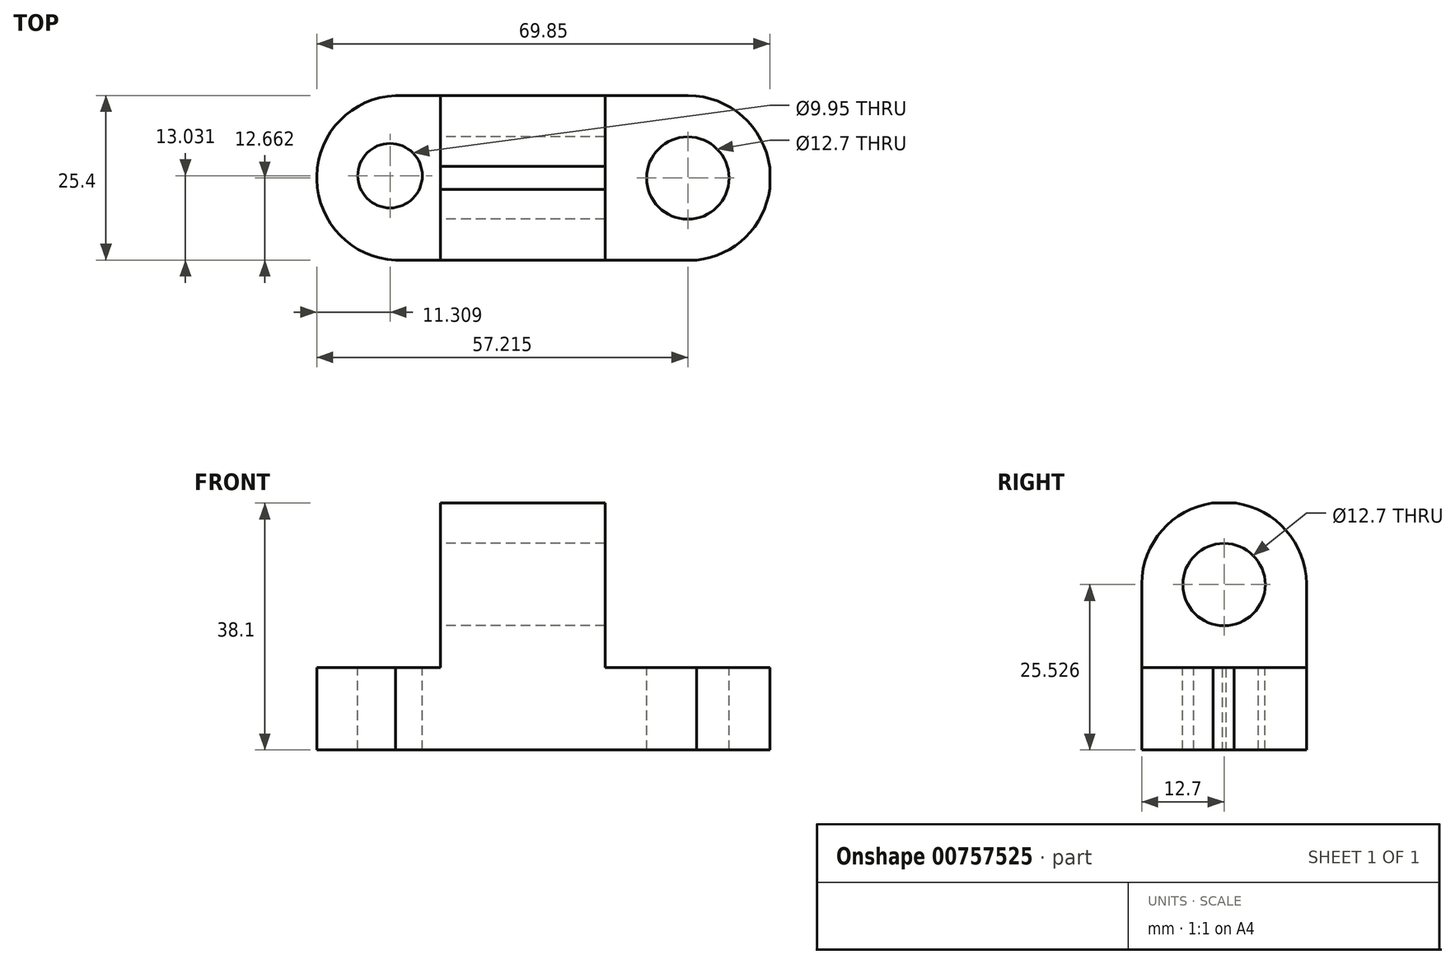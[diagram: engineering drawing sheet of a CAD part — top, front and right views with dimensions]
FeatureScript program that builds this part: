
annotation { "Feature Type Name" : "Feature", "Feature Type Description" : "" }
export const myFeature = defineFeature(function(context is Context, id is Id, definition is map)
    precondition{}
    {
        {
            var Q0;
            Q0=qCreatedBy(makeId("Front.planeOp"),FACE);
            var sketch = newSketch(context, id + "F0", { "sketchPlane" : qUnion([Q0])});
            skLineSegment(sketch, "E0", {"start": v(0, 0) * mm, "end": v(-69.85, 0) * mm});
            skLineSegment(sketch, "E1", {"start": v(-69.85, 0) * mm, "end": v(-69.85, 12.7) * mm});
            skLineSegment(sketch, "E2", {"start": v(-69.85, 12.7) * mm, "end": v(-50.8, 12.7) * mm});
            skLineSegment(sketch, "E3", {"start": v(-50.8, 12.7) * mm, "end": v(-50.8, 38.1) * mm});
            skLineSegment(sketch, "E4", {"start": v(-50.8, 38.1) * mm, "end": v(-25.4, 38.1) * mm});
            skLineSegment(sketch, "E5", {"start": v(-25.4, 38.1) * mm, "end": v(-25.4, 12.7) * mm});
            skLineSegment(sketch, "E6", {"start": v(-25.4, 12.7) * mm, "end": v(0, 12.7) * mm});
            skLineSegment(sketch, "E7", {"start": v(0, 12.7) * mm, "end": v(0, 0) * mm});
            skSolve(sketch);
        }
        {
            var Q0;
            Q0 = qSketchRegion(id + "F0", true);
            extrude(context, id + "F1", {"entities" : qUnion([Q0]), "depth" : 25.4 * mm, "offsetDistance" : 25.4 * mm});
        }
        {
            var Q0;
            Q0=makeQuery(id+"F1.opExtrude","SWEPT_FACE",FACE,{"disambiguationData":[OSD([sQuery(id+"F0.wireOp",EDGE,"E0")])]});
            var sketch = newSketch(context, id + "F2", { "sketchPlane" : qUnion([Q0])});
            skArc(sketch, "E8", {"start": v(-12.7, 0) * mm, "mid": v(0.09, 13.4) * mm, "end": v(-14.02, 25.4) * mm});
            skArc(sketch, "E9", {"start": v(-56.58, 25.4) * mm, "mid": v(-69.84, 13.24) * mm, "end": v(-57.66, 0) * mm});
            skSolve(sketch);
        }
        {
            var Q0;
            {var subQ0=sQuery(id+"F2.wireOp",EDGE,"E8");var subQ1=sQuery(id+"F0.wireOp",EDGE,"E0");var subQ4=makeQuery(id+"F1.opExtrude","CAP_EDGE",EDGE,{"disambiguationData":[OSD([subQ1])],"isStart":false});var subQ5=makeQuery(id+"F2.imprint","INTERSECT",VERTEX,{"disambiguationData":[OD(1.0)],"derivedFrom":[subQ4,subQ0]});Q0=makeQuery(id+"F2.imprint","IMPRINT",FACE,{"disambiguationData":[TD([[makeQuery(id+"F2.imprint","IMPRINT",EDGE,{"disambiguationData":[TD([[subQ5,1.0]])],"derivedFrom":subQ0}),-1.0]])]});}
            var Q1;
            {var subQ0=sQuery(id+"F2.wireOp",EDGE,"E8");var subQ1=sQuery(id+"F0.wireOp",EDGE,"E0");var subQ2=makeQuery(id+"F1.opExtrude","CAP_EDGE",EDGE,{"disambiguationData":[OSD([subQ1])],"isStart":true});var subQ3=makeQuery(id+"F2.imprint","INTERSECT",VERTEX,{"disambiguationData":[OD(1.0)],"derivedFrom":[subQ2,subQ0]});Q1=makeQuery(id+"F2.imprint","IMPRINT",FACE,{"disambiguationData":[TD([[makeQuery(id+"F2.imprint","IMPRINT",EDGE,{"disambiguationData":[TD([[subQ3,-1.0]])],"derivedFrom":subQ0}),-1.0]])]});}
            var Q2;
            {var subQ0=sQuery(id+"F2.wireOp",EDGE,"E9");var subQ1=sQuery(id+"F0.wireOp",EDGE,"E0");var subQ2=makeQuery(id+"F1.opExtrude","CAP_EDGE",EDGE,{"disambiguationData":[OSD([subQ1])],"isStart":true});var subQ3=makeQuery(id+"F2.imprint","INTERSECT",VERTEX,{"derivedFrom":[subQ2,subQ0]});Q2=makeQuery(id+"F2.imprint","IMPRINT",FACE,{"disambiguationData":[TD([[makeQuery(id+"F2.imprint","IMPRINT",EDGE,{"disambiguationData":[TD([[subQ3,1.0]])],"derivedFrom":subQ0}),-1.0]])]});}
            var Q3;
            {var subQ0=sQuery(id+"F2.wireOp",EDGE,"E9");var subQ1=sQuery(id+"F0.wireOp",EDGE,"E0");var subQ2=makeQuery(id+"F1.opExtrude","CAP_EDGE",EDGE,{"disambiguationData":[OSD([subQ1])],"isStart":false});var subQ3=makeQuery(id+"F2.imprint","INTERSECT",VERTEX,{"disambiguationData":[OD(1.0)],"derivedFrom":[subQ2,subQ0]});Q3=makeQuery(id+"F2.imprint","IMPRINT",FACE,{"disambiguationData":[TD([[makeQuery(id+"F2.imprint","IMPRINT",EDGE,{"disambiguationData":[TD([[subQ3,-1.0]])],"derivedFrom":subQ0}),-1.0]])]});}
            extrude(context, id + "F3", {"entities" : qUnion([Q0, Q1, Q2, Q3]), "operationType" : NewBodyOperationType.REMOVE, "endBound" : BoundingType.THROUGH_ALL, "oppositeDirection" : true, "depth" : 25.4 * mm, "offsetDistance" : 25.4 * mm});
        }
        {
            var Q0;
            Q0=makeQuery(id+"F1.opExtrude","SWEPT_FACE",FACE,{"disambiguationData":[OSD([sQuery(id+"F0.wireOp",EDGE,"E5")])]});
            var sketch = newSketch(context, id + "F4", { "sketchPlane" : qUnion([Q0])});
            skArc(sketch, "E10", {"start": v(0, 25.4) * mm, "mid": v(-12.7, 38.23) * mm, "end": v(-25.4, 25.4) * mm});
            skSolve(sketch);
        }
        {
            var Q0;
            {var subQ0=sQuery(id+"F4.wireOp",EDGE,"E10");var subQ1=sQuery(id+"F0.wireOp",EDGE,"E5");var subQ4=makeQuery(id+"F1.opExtrude","CAP_EDGE",EDGE,{"disambiguationData":[OSD([subQ1])],"isStart":false});var subQ5=makeQuery(id+"F4.imprint","INTERSECT",VERTEX,{"disambiguationData":[OD(1.0)],"derivedFrom":[subQ4,subQ0]});Q0=makeQuery(id+"F4.imprint","IMPRINT",FACE,{"disambiguationData":[TD([[makeQuery(id+"F4.imprint","IMPRINT",EDGE,{"disambiguationData":[TD([[subQ5,1.0]])],"derivedFrom":subQ0}),-1.0]])]});}
            var Q1;
            {var subQ0=sQuery(id+"F4.wireOp",EDGE,"E10");var subQ1=sQuery(id+"F0.wireOp",EDGE,"E5");var subQ2=makeQuery(id+"F1.opExtrude","CAP_EDGE",EDGE,{"disambiguationData":[OSD([subQ1])],"isStart":true});var subQ3=makeQuery(id+"F4.imprint","INTERSECT",VERTEX,{"disambiguationData":[OD(1.0)],"derivedFrom":[subQ2,subQ0]});Q1=makeQuery(id+"F4.imprint","IMPRINT",FACE,{"disambiguationData":[TD([[makeQuery(id+"F4.imprint","IMPRINT",EDGE,{"disambiguationData":[TD([[subQ3,-1.0]])],"derivedFrom":subQ0}),-1.0]])]});}
            extrude(context, id + "F5", {"entities" : qUnion([Q0, Q1]), "operationType" : NewBodyOperationType.REMOVE, "endBound" : BoundingType.THROUGH_ALL, "oppositeDirection" : true, "depth" : 25.4 * mm, "offsetDistance" : 25.4 * mm});
        }
        {
            var Q0;
            Q0=makeQuery(id+"F1.opExtrude","SWEPT_FACE",FACE,{"disambiguationData":[OSD([sQuery(id+"F0.wireOp",EDGE,"E3")])]});
            var sketch = newSketch(context, id + "F6", { "sketchPlane" : qUnion([Q0])});
            skCircle(sketch, "E11", {"center": v(12.7, 25.53) * mm, "radius": 6.35 * mm});
            skSolve(sketch);
        }
        {
            var Q0;
            Q0 = qSketchRegion(id + "F6", true);
            extrude(context, id + "F7", {"entities" : qUnion([Q0]), "operationType" : NewBodyOperationType.REMOVE, "endBound" : BoundingType.THROUGH_ALL, "oppositeDirection" : true, "depth" : 25.4 * mm, "offsetDistance" : 25.4 * mm});
        }
        {
            var Q0;
            Q0=makeQuery(id+"F1.opExtrude","SWEPT_FACE",FACE,{"disambiguationData":[OSD([sQuery(id+"F0.wireOp",EDGE,"E6")])]});
            var sketch = newSketch(context, id + "F8", { "sketchPlane" : qUnion([Q0])});
            skCircle(sketch, "E12", {"center": v(-12.63, -12.74) * mm, "radius": 6.35 * mm});
            skCircle(sketch, "E13", {"center": v(-58.54, -12.37) * mm, "radius": 4.97 * mm});
            skSolve(sketch);
        }
        {
            var Q0;
            Q0=makeQuery(id+"F8.imprint","IMPRINT",FACE,{"disambiguationData":[TD([[makeQuery(id+"F8.imprint","IMPRINT",EDGE,{"derivedFrom":sQuery(id+"F8.wireOp",EDGE,"E12")}),1.0]])]});
            var Q1;
            Q1=makeQuery(id+"F8.imprint","IMPRINT",FACE,{"disambiguationData":[TD([[makeQuery(id+"F8.imprint","IMPRINT",EDGE,{"derivedFrom":sQuery(id+"F8.wireOp",EDGE,"E13")}),1.0]])]});
            extrude(context, id + "F9", {"entities" : qUnion([Q0, Q1]), "operationType" : NewBodyOperationType.REMOVE, "endBound" : BoundingType.THROUGH_ALL, "oppositeDirection" : true, "depth" : 25.4 * mm, "offsetDistance" : 25.4 * mm});
        }
    });
